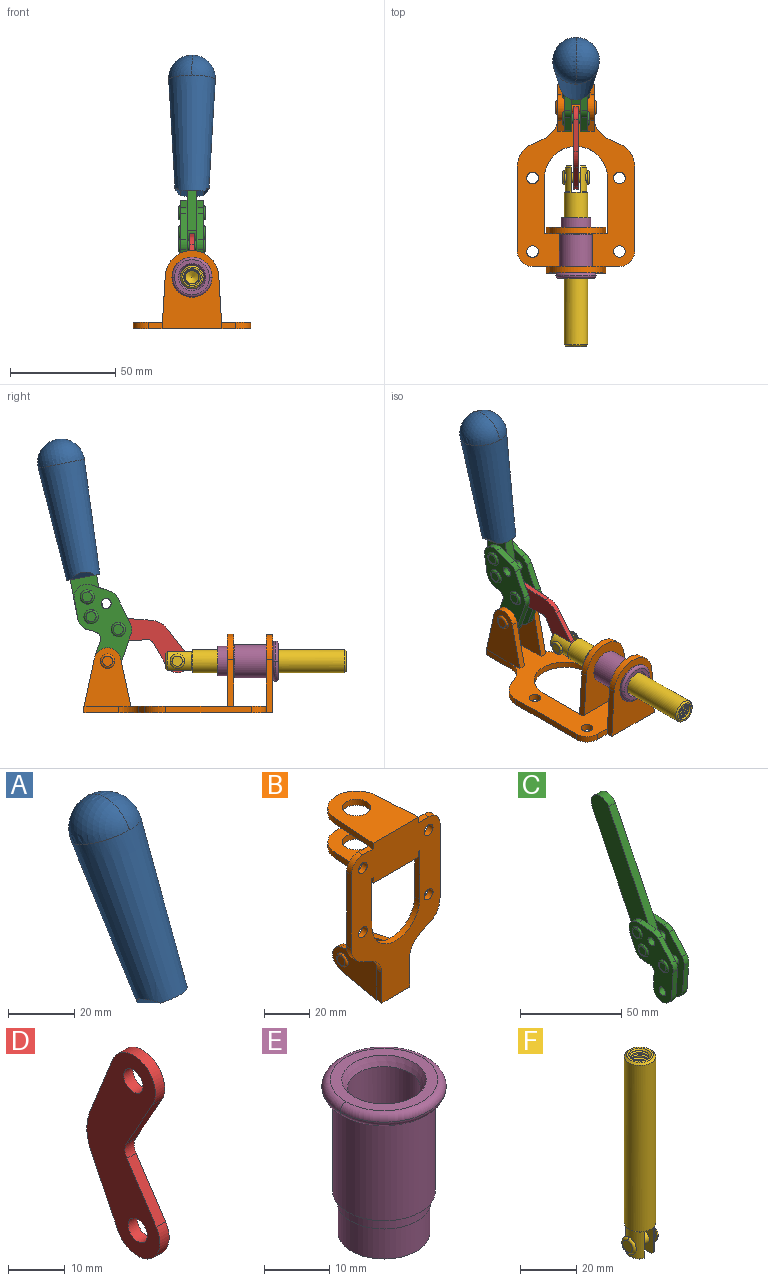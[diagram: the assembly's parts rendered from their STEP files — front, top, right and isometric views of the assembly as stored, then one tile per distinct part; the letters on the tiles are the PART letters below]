
ASSEMBLY  parts=6 mates=6
PART A: 11 faces, bbox 22.3x42.6x64.5 mm
  f0: sphere r=11.13mm, area 411.4mm2, adj f1,f8
  f1: cone r=11.11mm half-angle=3.3deg, axis (0,0.44,0.9), area 3251.8mm2, adj f0,f7,f8,f9,f10
  f2: cylinder r=6.16mm len=11.7mm, axis (1,0,0), area 89.5mm2, adj f3,f4,f5,f6
  f3: plane 60.23x36.75mm, normal (-1,0,0), area 763.6mm2, adj f2,f4,f6,f10
  f4: plane 51.37x25.05mm, normal (0,0.9,-0.44), area 264.2mm2, adj f2,f3,f5,f10
  f5: plane 60.23x36.75mm, normal (1,0,0), area 763.6mm2, adj f2,f4,f6,f10
  f6: plane 51.37x25.05mm, normal (0,-0.9,0.44), area 264.2mm2, adj f2,f3,f5,f10
  f7: plane 9.95x5.95mm, normal (0.71,-0.31,-0.64), area 25.8mm2, adj f1,f10
  f8: sphere r=11.13mm, area 411.4mm2, adj f0,f1
  f9: plane 9.95x5.95mm, normal (-0.71,-0.31,-0.64), area 25.8mm2, adj f1,f10
  f10: plane 14.27x11.38mm, normal (0,-0.44,-0.9), area 106.7mm2, adj f1,f3,f4,f5,f6,f7,f9
PART B: 55 faces, bbox 55.7x37.4x89.8 mm
  f0: torus R=2.41mm, axis (-1,0,0), area 15mm2, adj f11,f15,f25
  f1: torus R=2.41mm, axis (-1,0,0), area 15mm2, adj f10,f12,f22
  f2: cylinder r=2.78mm len=5.56mm, axis (0,-1,0), area 54.2mm2, adj f30,f54
  f3: cylinder r=14.99mm len=29.97mm, axis (0,-1,0), area 145.9mm2, adj f30,f49,f53,f54
  f4: cylinder r=2.78mm len=5.56mm, axis (0,-1,0), area 54.2mm2, adj f30,f54
  f5: cylinder r=2.78mm len=5.56mm, axis (0,-1,0), area 54.2mm2, adj f30,f54
  f6: cylinder r=2.78mm len=5.56mm, axis (0,-1,0), area 54.2mm2, adj f30,f54
  f7: cylinder r=6.35mm len=12.7mm, axis (0,0,1), area 123.6mm2, adj f27,f51
  f8: cylinder r=6.35mm len=12.7mm, axis (0,0,-1), area 124.7mm2, adj f21,f35
  f9: cylinder r=2.41mm len=11.18mm, axis (-1,0,0), area 169.4mm2, adj f16,f19
  f10: plane 4.83x4.83mm, normal (1,0,0), area 18.3mm2, adj f1,f12
  f11: plane 4.83x4.83mm, normal (-1,0,0), area 18.3mm2, adj f0,f15
  f12: torus R=2.41mm, axis (-1,0,0), area 15mm2, adj f1,f10,f22
  f13: cylinder r=6.35mm len=12.41mm, axis (1,0,0), area 53.4mm2, adj f18,f19,f22,f23
  f14: cylinder r=6.35mm len=12.41mm, axis (-1,0,0), area 53.4mm2, adj f16,f17,f24,f25
  f15: torus R=2.41mm, axis (-1,0,0), area 15mm2, adj f0,f11,f25
  f16: plane 27.86x22.35mm, normal (1,0,0), area 425.4mm2, adj f9,f14,f17,f24,f30
  f17: plane 22.86x4.97mm, normal (0,0.21,0.98), area 72.5mm2, adj f14,f16,f25,f30
  f18: plane 22.86x4.97mm, normal (0,0.21,0.98), area 72.5mm2, adj f13,f19,f22,f30
  f19: plane 27.86x22.35mm, normal (-1,0,0), area 425.4mm2, adj f9,f13,f18,f23,f30
  f20: cylinder r=12.7mm len=25.35mm, axis (0,0,-1), area 119.8mm2, adj f21,f34,f35,f36
  f21: plane 34.21x28.07mm, normal (0,0,-1), area 702.4mm2, adj f8,f20,f30,f34,f36
  f22: plane 27.96x22.45mm, normal (1,0,0), area 407.2mm2, adj f1,f12,f13,f18,f23,f30,f42,f43
  f23: plane 22.86x4.97mm, normal (0,0.21,-0.98), area 72.5mm2, adj f13,f19,f22,f44
  f24: plane 22.86x4.97mm, normal (0,0.21,-0.98), area 72.5mm2, adj f14,f16,f25,f44
  f25: plane 27.86x22.35mm, normal (-1,0,0), area 407.1mm2, adj f0,f14,f15,f17,f24,f30,f45,f46
  f26: plane 3.1x0.95mm, normal (0,0,-1), area 2.7mm2, adj f30,f49,f50,f54
  f27: plane 34.21x28.07mm, normal (0,0,1), area 702.4mm2, adj f7,f28,f30,f50,f52
  f28: cylinder r=12.7mm len=25.35mm, axis (0,0,1), area 118.8mm2, adj f27,f50,f51,f52
  f29: plane 3.1x0.95mm, normal (0,0,-1), area 2.7mm2, adj f30,f52,f53,f54
  f30: plane 86.54x55.63mm, normal (0,1,0), area 2362.9mm2, adj f2,f3,f4,f5,f6,f16,f17,f18
  f31: plane 40.56x3.1mm, normal (-1,0,0), area 125.7mm2, adj f30,f32,f48,f54
  f32: cylinder r=7.11mm len=7.11mm, axis (0,-1,0), area 34.6mm2, adj f30,f31,f33,f54
  f33: plane 6.67x3.1mm, normal (0,0,1), area 20.4mm2, adj f30,f32,f34,f54
  f34: plane 25.39x3.13mm, normal (-1,0.06,0), area 79.5mm2, adj f20,f21,f33,f35,f54
  f35: plane 37.31x28.45mm, normal (0,0,1), area 789.9mm2, adj f8,f20,f34,f36,f54
  f36: plane 25.39x3.13mm, normal (1,0.06,0), area 79.5mm2, adj f20,f21,f35,f37,f54
  f37: plane 6.67x3.1mm, normal (0,0,1), area 20.4mm2, adj f30,f36,f38,f54
  f38: cylinder r=7.11mm len=7.11mm, axis (0,-1,0), area 34.6mm2, adj f30,f37,f39,f54
  f39: plane 40.56x3.1mm, normal (1,0,0), area 125.7mm2, adj f30,f38,f40,f54
  f40: cylinder r=11.18mm len=10.16mm, axis (0,-1,0), area 39.5mm2, adj f30,f39,f41,f54
  f41: plane 6.09x3.1mm, normal (0.42,0,-0.91), area 20.8mm2, adj f30,f40,f42,f54
  f42: cylinder r=11.18mm len=9.41mm, axis (0,-1,0), area 37.2mm2, adj f22,f30,f41,f43,f54
  f43: plane 16.5x3.1mm, normal (1,0,0), area 51.1mm2, adj f22,f42,f44,f54
  f44: plane 17.37x3.1mm, normal (0,0,-1), area 53.8mm2, adj f23,f24,f30,f43,f45,f54
  f45: plane 16.5x3.1mm, normal (-1,0,0), area 51.1mm2, adj f25,f44,f46,f54
  f46: cylinder r=11.18mm len=9.41mm, axis (0,-1,0), area 37.2mm2, adj f25,f30,f45,f47,f54
  f47: plane 6.09x3.1mm, normal (-0.42,0,-0.91), area 20.8mm2, adj f30,f46,f48,f54
  f48: cylinder r=11.18mm len=10.16mm, axis (0,-1,0), area 39.5mm2, adj f30,f31,f47,f54
  f49: plane 26.54x3.1mm, normal (-1,0,0), area 82.3mm2, adj f3,f26,f30,f54
  f50: plane 25.39x3.1mm, normal (1,0.06,0), area 78.8mm2, adj f26,f27,f28,f51,f54
  f51: plane 37.31x28.45mm, normal (0,0,-1), area 789.9mm2, adj f7,f28,f50,f52,f54
  f52: plane 25.39x3.1mm, normal (-1,0.06,0), area 78.8mm2, adj f27,f28,f29,f51,f54
  f53: plane 26.54x3.1mm, normal (1,0,0), area 82.3mm2, adj f3,f29,f30,f54
  f54: plane 89.66x55.63mm, normal (0,-1,0), area 2678.5mm2, adj f2,f3,f4,f5,f6,f26,f29,f31
PART C: 59 faces, bbox 12.9x60.2x99.6 mm
  f0: torus R=2.39mm, axis (-1,0,0), area 14.9mm2, adj f20,f43,f51
  f1: torus R=2.39mm, axis (-1,0,0), area 14.9mm2, adj f19,f42,f51
  f2: torus R=2.39mm, axis (-1,0,0), area 14.9mm2, adj f18,f35,f51
  f3: torus R=2.39mm, axis (-1,0,0), area 14.9mm2, adj f14,f17,f23
  f4: torus R=2.39mm, axis (-1,0,0), area 14.9mm2, adj f13,f16,f23
  f5: torus R=2.39mm, axis (-1,0,0), area 14.9mm2, adj f12,f15,f23
  f6: cylinder r=2.39mm len=4.78mm, axis (1,0,0), area 46.5mm2, adj f48,f50,f51
  f7: cylinder r=2.39mm len=4.78mm, axis (1,0,0), area 46.5mm2, adj f50,f51
  f8: cylinder r=6.35mm len=12.68mm, axis (1,0,0), area 61.8mm2, adj f38,f39,f50,f51
  f9: cylinder r=2.39mm len=4.78mm, axis (-1,0,0), area 70.5mm2, adj f46,f50
  f10: cylinder r=2.39mm len=4.78mm, axis (-1,0,0), area 46.5mm2, adj f23,f45,f46
  f11: cylinder r=2.39mm len=4.78mm, axis (-1,0,0), area 46.5mm2, adj f23,f46
  f12: plane 4.78x4.78mm, normal (1,0,0), area 17.9mm2, adj f5,f15
  f13: plane 4.78x4.78mm, normal (1,0,0), area 17.9mm2, adj f4,f16
  f14: plane 4.78x4.78mm, normal (1,0,0), area 17.9mm2, adj f3,f17
  f15: torus R=2.39mm, axis (-1,0,0), area 14.9mm2, adj f5,f12,f23
  f16: torus R=2.39mm, axis (-1,0,0), area 14.9mm2, adj f4,f13,f23
  f17: torus R=2.39mm, axis (-1,0,0), area 14.9mm2, adj f3,f14,f23
  f18: plane 4.78x4.78mm, normal (-1,0,0), area 17.9mm2, adj f2,f35
  f19: plane 4.78x4.78mm, normal (-1,0,0), area 17.9mm2, adj f1,f42
  f20: plane 4.78x4.78mm, normal (-1,0,0), area 17.9mm2, adj f0,f43
  f21: plane 2.26x0.2mm, normal (1,0,0), area 0.2mm2, adj f31,f44
  f22: plane 2.26x0.2mm, normal (-1,0,0), area 0.2mm2, adj f41,f44
  f23: plane 39.37x30.77mm, normal (1,0,0), area 565.5mm2, adj f3,f4,f5,f10,f11,f15,f16,f17
  f24: cylinder r=6.1mm len=4.15mm, axis (-1,0,0), area 14.7mm2, adj f23,f25,f32,f46
  f25: plane 10.25x9.01mm, normal (0,-0.75,0.66), area 42.3mm2, adj f23,f24,f26,f46
  f26: cylinder r=6.35mm len=4.64mm, axis (-1,0,0), area 15.6mm2, adj f23,f25,f27,f46
  f27: plane 15.84x3.1mm, normal (0,-1,-0.07), area 49.2mm2, adj f23,f26,f28,f46
  f28: cylinder r=6.35mm len=12.68mm, axis (-1,0,0), area 61.8mm2, adj f23,f27,f29,f46
  f29: plane 8.11x3.1mm, normal (0,1,0.07), area 25.2mm2, adj f23,f28,f30,f46
  f30: cylinder r=3.05mm len=3.25mm, axis (-1,0,0), area 14.8mm2, adj f23,f29,f31,f46
  f31: plane 5.99x3.1mm, normal (0,0.07,-1), area 18.6mm2, adj f21,f23,f30,f44,f46
  f32: plane 9.5x3.1mm, normal (0,-0.07,1), area 29.5mm2, adj f23,f24,f33,f46,f47
  f33: cylinder r=6.1mm len=8.63mm, axis (-1,0,0), area 39.1mm2, adj f23,f32,f34,f47
  f34: plane 8.65x3.96mm, normal (0,0.91,-0.42), area 29.5mm2, adj f23,f33,f44,f47
  f35: torus R=2.39mm, axis (-1,0,0), area 14.9mm2, adj f2,f18,f51
  f36: plane 10.25x9.01mm, normal (0,-0.75,0.66), area 42.3mm2, adj f37,f49,f50,f51
  f37: cylinder r=6.35mm len=4.64mm, axis (1,0,0), area 15.6mm2, adj f36,f38,f50,f51
  f38: plane 15.84x3.1mm, normal (0,-1,-0.07), area 49.2mm2, adj f8,f37,f50,f51
  f39: plane 8.11x3.1mm, normal (0,1,0.07), area 25.2mm2, adj f8,f40,f50,f51
  f40: cylinder r=3.05mm len=3.25mm, axis (1,0,0), area 14.8mm2, adj f39,f41,f50,f51
  f41: plane 5.99x3.1mm, normal (0,0.07,-1), area 18.6mm2, adj f22,f40,f44,f50,f51
  f42: torus R=2.39mm, axis (-1,0,0), area 14.9mm2, adj f1,f19,f51
  f43: torus R=2.39mm, axis (-1,0,0), area 14.9mm2, adj f0,f20,f51
  f44: cylinder r=6.35mm len=12.12mm, axis (-1,0,0), area 128.9mm2, adj f21,f22,f23,f31,f34,f41,f46,f47
  f45: plane 2.65x1.35mm, normal (1,0,0), area 1mm2, adj f10,f55
  f46: plane 39.08x20.42mm, normal (-1,0,0), area 412.5mm2, adj f9,f10,f11,f24,f25,f26,f27,f28
  f47: plane 77.62x39.82mm, normal (1,0,0), area 850mm2, adj f32,f33,f34,f44,f53,f54,f55
  f48: plane 2.65x1.35mm, normal (-1,0,0), area 1mm2, adj f6,f55
  f49: cylinder r=6.1mm len=4.15mm, axis (1,0,0), area 14.7mm2, adj f36,f50,f51,f56
  f50: plane 39.08x20.42mm, normal (1,0,0), area 412.5mm2, adj f6,f7,f8,f9,f36,f37,f38,f39
  f51: plane 39.37x30.77mm, normal (-1,0,0), area 565.5mm2, adj f0,f1,f2,f6,f7,f8,f35,f36
  f52: plane 8.65x3.96mm, normal (0,0.91,-0.42), area 29.5mm2, adj f44,f51,f57,f58
  f53: plane 68.49x33.4mm, normal (0,0.9,-0.44), area 358.1mm2, adj f44,f47,f54,f58
  f54: cylinder r=6.35mm len=12.06mm, axis (1,0,0), area 93.7mm2, adj f47,f53,f55,f58
  f55: plane 68.49x33.4mm, normal (0,-0.9,0.44), area 358.1mm2, adj f44,f45,f46,f47,f48,f50,f54,f58
  f56: plane 9.5x3.1mm, normal (0,-0.07,1), area 29.5mm2, adj f49,f50,f51,f57,f58
  f57: cylinder r=6.1mm len=8.63mm, axis (1,0,0), area 39.1mm2, adj f51,f52,f56,f58
  f58: plane 77.62x39.82mm, normal (-1,0,0), area 850mm2, adj f44,f52,f53,f54,f55,f56,f57
PART D: 12 faces, bbox 2.3x18.2x42.8 mm
  f0: cylinder r=2.4mm len=4.8mm, axis (1,0,0), area 34.9mm2, adj f4,f11
  f1: cylinder r=10.41mm len=8.47mm, axis (1,0,0), area 20.2mm2, adj f4,f9,f10,f11
  f2: cylinder r=3.05mm len=3.16mm, axis (1,0,0), area 7.7mm2, adj f4,f6,f7,f11
  f3: cylinder r=2.4mm len=4.8mm, axis (1,0,0), area 34.9mm2, adj f4,f11
  f4: plane 42.81x18.23mm, normal (-1,0,0), area 414.1mm2, adj f0,f1,f2,f3,f5,f6,f7,f8
  f5: cylinder r=5.54mm len=10.67mm, axis (1,0,0), area 41.8mm2, adj f4,f6,f10,f11
  f6: plane 11.66x6.53mm, normal (0,-0.87,-0.49), area 30.9mm2, adj f2,f4,f5,f11
  f7: plane 11.17x7.33mm, normal (0,-0.84,0.55), area 30.9mm2, adj f2,f4,f8,f11
  f8: cylinder r=5.54mm len=10.51mm, axis (1,0,0), area 41.8mm2, adj f4,f7,f9,f11
  f9: plane 13.67x6.67mm, normal (0,0.9,-0.44), area 35.1mm2, adj f1,f4,f8,f11
  f10: plane 14.1x5.7mm, normal (0,0.93,0.37), area 35.1mm2, adj f1,f4,f5,f11
  f11: plane 42.81x18.23mm, normal (1,0,0), area 414.1mm2, adj f0,f1,f2,f3,f5,f6,f7,f8
PART E: 15 faces, bbox 20.6x20.6x28.7 mm
  f0: torus R=8.26mm, axis (0,0,1), area 56.8mm2, adj f1,f10,f12
  f1: torus R=8.26mm, axis (0,0,1), area 56.8mm2, adj f0,f6,f13
  f2: cylinder r=5.59mm len=25.91mm, axis (0,0,1), area 909.6mm2, adj f3,f4
  f3: cone r=6.86mm half-angle=45deg, axis (0,0,-1), area 70.2mm2, adj f2,f14
  f4: cone r=6.47mm half-angle=30deg, axis (0,0,1), area 66.7mm2, adj f2,f13
  f5: cylinder r=7.04mm len=14.07mm, axis (0,0,1), area 252.6mm2, adj f11,f14
  f6: torus R=8.26mm, axis (0,0,1), area 56.8mm2, adj f1,f12,f13
  f7: cylinder r=7.16mm len=14.33mm, axis (0,0,1), area 91.5mm2, adj f9,f11
  f8: cylinder r=7.86mm len=18.42mm, axis (0,0,1), area 909.6mm2, adj f9,f10
  f9: plane 15.72x15.72mm, normal (0,0,-1), area 33mm2, adj f7,f8
  f10: plane 16.51x16.51mm, normal (0,0,-1), area 19.9mm2, adj f0,f8,f12
  f11: plane 14.33x14.33mm, normal (0,0,-1), area 5.7mm2, adj f5,f7
  f12: torus R=8.26mm, axis (0,0,1), area 56.8mm2, adj f0,f6,f10
  f13: plane 16.51x16.51mm, normal (0,0,1), area 82.7mm2, adj f1,f4,f6
  f14: plane 14.07x14.07mm, normal (0,0,-1), area 7.8mm2, adj f3,f5
PART F: 48 faces, bbox 12.6x11.1x86.1 mm
  f0: torus R=2.41mm, axis (-1,0,0), area 15mm2, adj f30,f32,f34
  f1: torus R=2.41mm, axis (-1,0,0), area 15mm2, adj f29,f31,f33
  f2: cylinder r=5.54mm len=72.39mm, axis (0,0,1), area 2518.5mm2, adj f3,f4,f42,f43
  f3: cone r=5.54mm half-angle=45deg, axis (0,0,1), area 7.6mm2, adj f2,f5,f41
  f4: cone r=5.54mm half-angle=45deg, axis (0,0,-1), area 34.9mm2, adj f2,f39
  f5: cylinder r=5.08mm len=11.48mm, axis (0,0,1), area 108.3mm2, adj f3,f7,f8,f41
  f6: cylinder r=2.41mm len=4.83mm, axis (-1,0,0), area 71.2mm2, adj f40,f41
  f7: cylinder r=2.41mm len=4.83mm, axis (-1,0,0), area 7.6mm2, adj f5,f34
  f8: cone r=5.08mm half-angle=45deg, axis (0,0,1), area 10.6mm2, adj f5,f37,f41
  f9: cone r=3.98mm half-angle=45deg, axis (0,0,1), area 17.6mm2, adj f27,f39,f45,f46,f47
  f10: cylinder r=2.41mm len=4.83mm, axis (-1,0,0), area 7.6mm2, adj f33,f38
  f11: cylinder r=3.2mm len=6.4mm, axis (0,0,1), area 78.4mm2, adj f12,f28,f44,f45,f47
  f12: cylinder r=3.2mm len=6.4mm, axis (0,0,1), area 10.5mm2, adj f11,f13,f45,f47
  f13: cylinder r=3.2mm len=6.4mm, axis (0,0,1), area 10.5mm2, adj f12,f14,f45,f47
  f14: cylinder r=3.2mm len=6.4mm, axis (0,0,1), area 10.5mm2, adj f13,f15,f45,f47
  f15: cylinder r=3.2mm len=6.4mm, axis (0,0,1), area 10.5mm2, adj f14,f16,f45,f47
  f16: cylinder r=3.2mm len=6.4mm, axis (0,0,1), area 10.5mm2, adj f15,f17,f45,f47
  f17: cylinder r=3.2mm len=6.4mm, axis (0,0,1), area 10.5mm2, adj f16,f18,f45,f47
  f18: cylinder r=3.2mm len=6.4mm, axis (0,0,1), area 10.5mm2, adj f17,f19,f45,f47
  f19: cylinder r=3.2mm len=6.4mm, axis (0,0,1), area 10.5mm2, adj f18,f20,f45,f47
  f20: cylinder r=3.2mm len=6.4mm, axis (0,0,1), area 10.5mm2, adj f19,f21,f45,f47
  f21: cylinder r=3.2mm len=6.4mm, axis (0,0,1), area 10.5mm2, adj f20,f22,f45,f47
  f22: cylinder r=3.2mm len=6.4mm, axis (0,0,1), area 10.5mm2, adj f21,f23,f45,f47
  f23: cylinder r=3.2mm len=6.4mm, axis (0,0,1), area 10.5mm2, adj f22,f24,f45,f47
  f24: cylinder r=3.2mm len=6.4mm, axis (0,0,1), area 10.5mm2, adj f23,f25,f45,f47
  f25: cylinder r=3.2mm len=6.4mm, axis (0,0,1), area 10.5mm2, adj f24,f26,f45,f47
  f26: cylinder r=3.2mm len=6.4mm, axis (0,0,1), area 10.5mm2, adj f25,f27,f45,f47
  f27: cylinder r=3.2mm len=6.4mm, axis (0,0,1), area 7.4mm2, adj f9,f26,f45,f47
  f28: cone r=3.2mm half-angle=60deg, axis (0,0,1), area 37.2mm2, adj f11
  f29: plane 4.83x4.83mm, normal (-1,0,0), area 18.3mm2, adj f1,f31
  f30: plane 4.83x4.83mm, normal (1,0,0), area 18.3mm2, adj f0,f32
  f31: torus R=2.41mm, axis (-1,0,0), area 15mm2, adj f1,f29,f33
  f32: torus R=2.41mm, axis (-1,0,0), area 15mm2, adj f0,f30,f34
  f33: plane 6.83x6.83mm, normal (1,0,0), area 18.3mm2, adj f1,f10,f31
  f34: plane 6.83x6.83mm, normal (-1,0,0), area 18.3mm2, adj f0,f7,f32
  f35: cone r=5.08mm half-angle=45deg, axis (0,0,1), area 10.6mm2, adj f36,f38,f40
  f36: plane 7.25x1.97mm, normal (0,0,-1), area 10mm2, adj f35,f40
  f37: plane 7.25x1.97mm, normal (0,0,-1), area 10mm2, adj f8,f41
  f38: cylinder r=5.08mm len=11.48mm, axis (0,0,1), area 108.3mm2, adj f10,f35,f40,f42
  f39: plane 9.55x9.55mm, normal (0,0,1), area 22mm2, adj f4,f9
  f40: plane 12.76x10.09mm, normal (1,0,0), area 95.7mm2, adj f6,f35,f36,f38,f42,f43
  f41: plane 12.76x10.09mm, normal (-1,0,0), area 95.7mm2, adj f3,f5,f6,f8,f37,f43
  f42: cone r=5.54mm half-angle=45deg, axis (0,0,1), area 7.6mm2, adj f2,f38,f40
  f43: plane 11.07x4.7mm, normal (0,0,-1), area 50.4mm2, adj f2,f40,f41
  f44: plane 0.89x0.62mm, normal (-1,0,0), area 0.3mm2, adj f11,f45,f46,f47
  f45: bspline ~24.8x7.63mm, area 266.6mm2, adj f9,f11,f12,f13,f14,f15,f16,f17
  f46: bspline ~24.87x7.63mm, area 73.6mm2, adj f9,f44,f45,f47
  f47: bspline ~24.98x7.63mm, area 272.5mm2, adj f9,f11,f12,f13,f14,f15,f16,f17
PLACE A rot(axis=(1,0,0),15deg) t=(0,9.32,46.14)mm
PLACE B rot(axis=(1,0,0),90deg) t=(0,9.31,-3.1)mm fixed
PLACE C rot(axis=(1,0,0),15deg) t=(0,9.32,46.14)mm
PLACE D rot(axis=(0,-0.53,-0.85),180deg) t=(0,33.22,7.61)mm
PLACE E rot(axis=(1,0,0),90deg) t=(0,9.31,-3.1)mm
PLACE F rot(axis=(1,0,0),90deg) t=(0,23.73,-3.1)mm
MATE slider F.f2 <-> B.f7  axis (0,-1,0) through (0,-35.05,21.51)mm
MATE fastened E.f0 <-> B.f7  axis (0,1,0) through (0,-37.09,21.51)mm
MATE revolute C.f7 <-> B.f0  axis (-1,0,0) through (0,41.4,21.51)mm
MATE fastened C.f54 <-> A.f2  axis (1,0,0) through (0,63.76,117.44)mm
MATE revolute C.f4 <-> D.f5  axis (-1,0,0) through (0,36.23,36.52)mm
MATE revolute D.f3 <-> F.f6  axis (-1,0,0) through (0,8.25,21.51)mm
